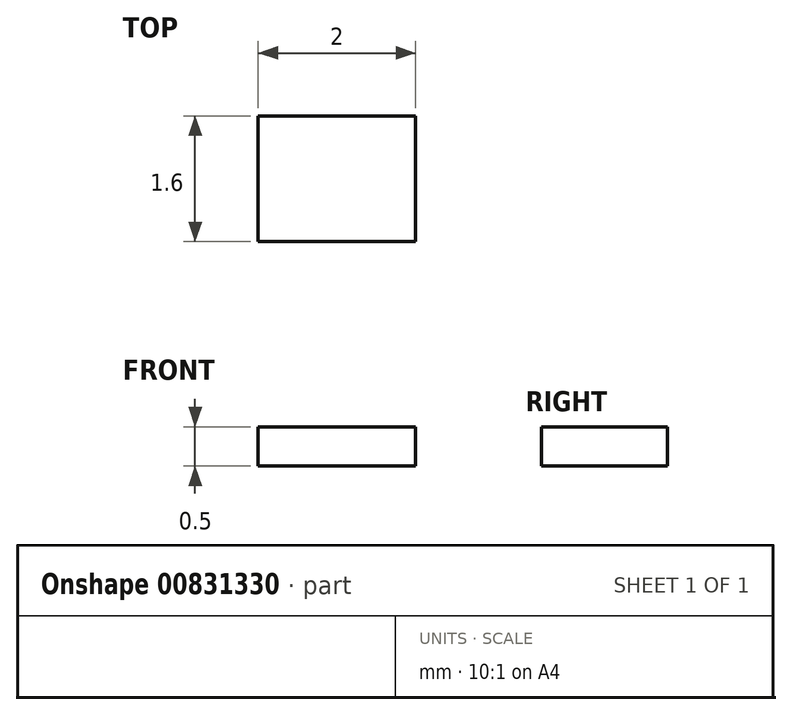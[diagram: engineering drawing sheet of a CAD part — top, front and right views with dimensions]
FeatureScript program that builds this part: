
annotation { "Feature Type Name" : "Feature", "Feature Type Description" : "" }
export const myFeature = defineFeature(function(context is Context, id is Id, definition is map)
    precondition{}
    {
        {
            var Q0;
            Q0=qCreatedBy(makeId("Top.planeOp"),FACE);
            var sketch = newSketch(context, id + "F0", { "sketchPlane" : qUnion([Q0])});
            skLineSegment(sketch, "E0.bottom", {"start": v(-1, -0.62) * mm, "end": v(1, -0.62) * mm});
            skLineSegment(sketch, "E0.top", {"start": v(-1, 0.62) * mm, "end": v(1, 0.62) * mm});
            skLineSegment(sketch, "E0.left", {"start": v(-1, -0.62) * mm, "end": v(-1, 0.62) * mm});
            skLineSegment(sketch, "E0.right", {"start": v(1, -0.62) * mm, "end": v(1, 0.62) * mm});
            skLineSegment(sketch, "E1", {"start": v(0, 0.62) * mm, "end": v(0, -0.62) * mm, "construction": true});
            skSolve(sketch);
        }
        {
            var Q0;
            Q0=qCreatedBy(makeId("Top.planeOp"),FACE);
            var sketch = newSketch(context, id + "F1", { "sketchPlane" : qUnion([Q0])});
            skLineSegment(sketch, "E2.bottom", {"start": v(-1, -0.8) * mm, "end": v(1, -0.8) * mm});
            skLineSegment(sketch, "E2.top", {"start": v(-1, 0.8) * mm, "end": v(1, 0.8) * mm});
            skLineSegment(sketch, "E2.left", {"start": v(-1, -0.8) * mm, "end": v(-1, 0.8) * mm});
            skLineSegment(sketch, "E2.right", {"start": v(1, -0.8) * mm, "end": v(1, 0.8) * mm});
            skLineSegment(sketch, "E3", {"start": v(0, 0.8) * mm, "end": v(0, -0.8) * mm, "construction": true});
            skSolve(sketch);
        }
        {
            var Q0;
            Q0=qCreatedBy(makeId("Top.planeOp"),FACE);
            var sketch = newSketch(context, id + "F2", { "sketchPlane" : qUnion([Q0])});
            skLineSegment(sketch, "E4.bottom", {"start": v(-1.6, 0.63) * mm, "end": v(-0.3, 0.63) * mm});
            skLineSegment(sketch, "E4.top", {"start": v(-1.6, -0.62) * mm, "end": v(-0.3, -0.62) * mm});
            skLineSegment(sketch, "E4.left", {"start": v(-1.6, 0.63) * mm, "end": v(-1.6, -0.63) * mm});
            skLineSegment(sketch, "E4.right", {"start": v(-0.3, 0.63) * mm, "end": v(-0.3, -0.63) * mm});
            skLineSegment(sketch, "E5.bottom", {"start": v(0.3, 0.63) * mm, "end": v(1.6, 0.63) * mm});
            skLineSegment(sketch, "E5.top", {"start": v(0.3, -0.62) * mm, "end": v(1.6, -0.62) * mm});
            skLineSegment(sketch, "E5.left", {"start": v(0.3, 0.63) * mm, "end": v(0.3, -0.63) * mm});
            skLineSegment(sketch, "E5.right", {"start": v(1.6, 0.63) * mm, "end": v(1.6, -0.63) * mm});
            skLineSegment(sketch, "E6", {"start": v(-0.3, 0) * mm, "end": v(0.3, 0) * mm, "construction": true});
            skSolve(sketch);
        }
        {
            var Q0;
            Q0 = qSketchRegion(id + "F0", true);
            extrude(context, id + "F3", {"entities" : qUnion([Q0]), "depth" : .1 * mm, "offsetDistance" : 25 * mm});
        }
        {
            var Q0;
            Q0 = qSketchRegion(id + "F1", true);
            extrude(context, id + "F4", {"entities" : qUnion([Q0]), "operationType" : NewBodyOperationType.ADD, "depth" : .5 * mm, "offsetDistance" : 25 * mm});
        }
    });
